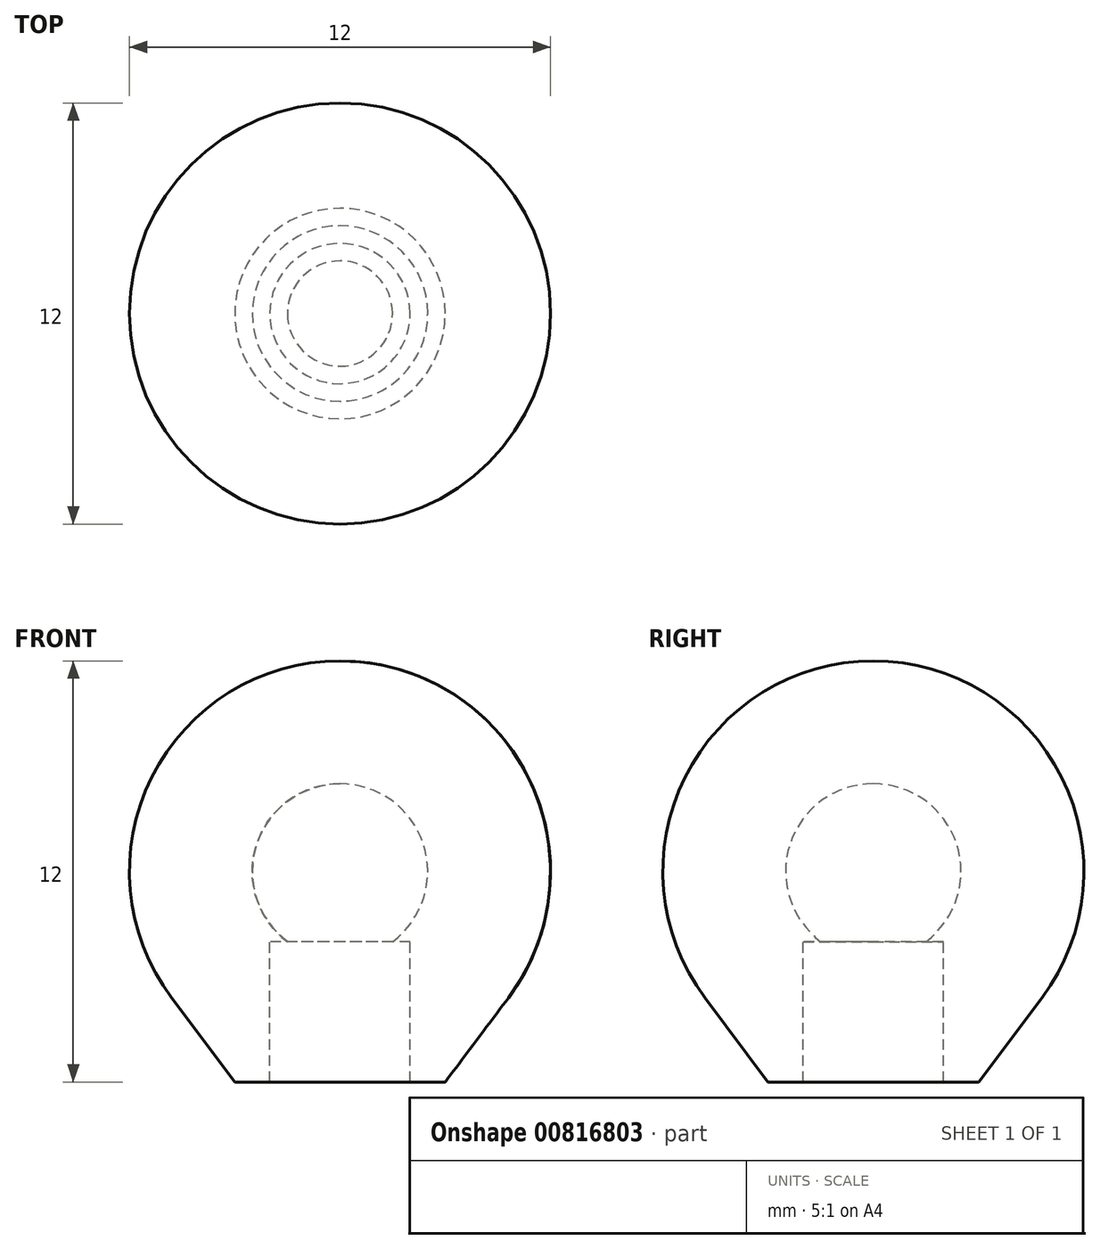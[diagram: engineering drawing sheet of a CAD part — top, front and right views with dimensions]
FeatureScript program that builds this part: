
annotation { "Feature Type Name" : "Feature", "Feature Type Description" : "" }
export const myFeature = defineFeature(function(context is Context, id is Id, definition is map)
    precondition{}
    {
        {
            var Q0;
            Q0=qCreatedBy(makeId("Front.planeOp"),FACE);
            var sketch = newSketch(context, id + "F0", { "sketchPlane" : qUnion([Q0])});
            skArc(sketch, "E0", {"start": v(0, 9.6) * mm, "mid": v(-5.37, 6.28) * mm, "end": v(-4.8, 0) * mm});
            skLineSegment(sketch, "E1", {"start": v(-4.8, 0) * mm, "end": v(-3, -2.4) * mm});
            skLineSegment(sketch, "E2", {"start": v(-3, -2.4) * mm, "end": v(-2, -2.4) * mm});
            skLineSegment(sketch, "E3", {"start": v(-2, -2.4) * mm, "end": v(-2, 1.6) * mm});
            skLineSegment(sketch, "E4", {"start": v(-2, 1.6) * mm, "end": v(-1.5, 1.6) * mm});
            skArc(sketch, "E5", {"start": v(0, 6.1) * mm, "mid": v(-2.37, 4.4) * mm, "end": v(-1.5, 1.6) * mm});
            skPoint(sketch, "E6.orphan", {"position": v(0, 1.6) * mm});
            skLineSegment(sketch, "E7", {"start": v(0, 9.6) * mm, "end": v(0, 6.1) * mm});
            skLineSegment(sketch, "E8", {"start": v(0, 0.87) * mm, "end": v(0, -8.37) * mm});
            skSolve(sketch);
        }
        {
            var Q0;
            Q0=makeQuery(id+"F0.imprint","IMPRINT",FACE,{"disambiguationData":[TD([[makeQuery(id+"F0.imprint","IMPRINT",EDGE,{"derivedFrom":sQuery(id+"F0.wireOp",EDGE,"E0")}),1.0]])]});
            var Q1;
            Q1=sQuery(id+"F0.wireOp",EDGE,"E8");
            revolve(context, id + "F1", {"surfaceOperationType" : NewSurfaceOperationType.NEW, "entities" : qUnion([Q0]), "axis" : qUnion([Q1]), "revolveType" : RevolveType.FULL});
        }
    });
